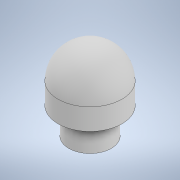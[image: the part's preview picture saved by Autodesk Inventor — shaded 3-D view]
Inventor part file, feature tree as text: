
AUTODESK INVENTOR PART (.ipt)
format: ipt  version: 2022 (Build 260153000, 153)  size: 142,336 bytes
history: native  units: in
note: dims shown in document units (in); Inventor stores cm internally (conversion verified against a paired STEP export)
features: revolve x1, sketch x1
ambient origin geometry x8: Origin, YZ Plane, XZ Plane, XY Plane, X Axis, Y Axis, Z Axis, Center Point
bodies: Solid1 (feature_tree)
feature tree (2):
  revolve  "Revolution1"  [1 undecoded]
  sketch  "Sketch1"  dims[d0=0.1575in d1=0.0787in d2=0.1969in d3=0.0787in d4=0.0394in d5=0.0394in d6=360.0deg]
note: 1 required parameter value undecoded (feature->parameter linkage not recoverable at this tier; creation-order binding heuristic only, values carry confidence <= 0.55)
